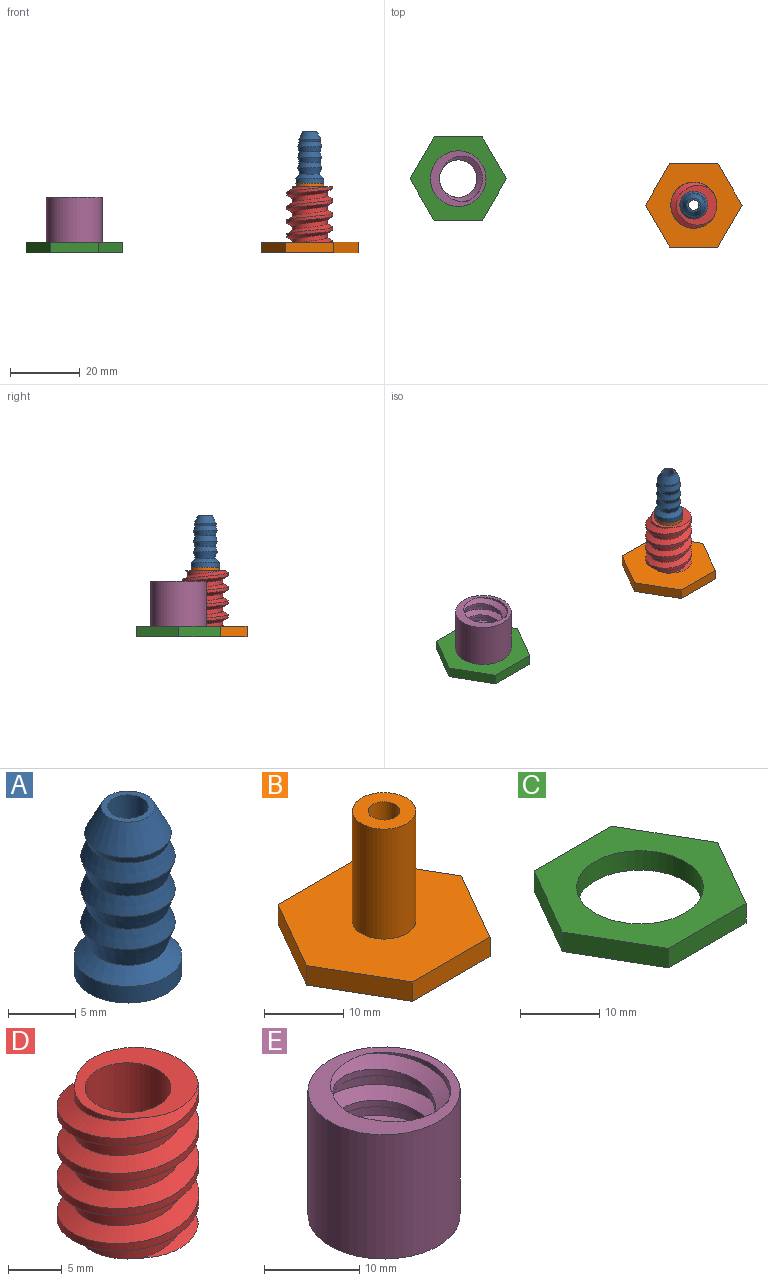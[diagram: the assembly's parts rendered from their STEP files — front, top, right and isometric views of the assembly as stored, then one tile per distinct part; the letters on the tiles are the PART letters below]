
ASSEMBLY  parts=5 mates=4
PART A: 14 faces, bbox 8x8x15 mm
  f0: cylinder r=4mm len=8mm, axis (0,0,1), area 37.7mm2, adj f2,f11
  f1: cylinder r=1.5mm len=14.2mm, axis (0,0,1), area 133.8mm2, adj f3,f12
  f2: plane 8x8mm, normal (0,0,-1), area 33.6mm2, adj f0,f12
  f3: plane 4x4mm, normal (0,0,1), area 5.5mm2, adj f1,f13
  f4: cone r=3.5mm half-angle=18.4deg, axis (0,0,1), area 12.9mm2, adj f6,f13
  f5: cone r=3.5mm half-angle=18.4deg, axis (0,0,1), area 32.3mm2, adj f6,f8
  f6: cone r=3mm half-angle=18.4deg, axis (0,0,-1), area 32.3mm2, adj f4,f5
  f7: cone r=3.5mm half-angle=18.4deg, axis (0,0,1), area 32.3mm2, adj f8,f10
  f8: cone r=3mm half-angle=18.4deg, axis (0,0,-1), area 32.3mm2, adj f5,f7
  f9: cone r=3.5mm half-angle=18.4deg, axis (0,0,1), area 39.6mm2, adj f10,f11
  f10: cone r=3mm half-angle=18.4deg, axis (0,0,-1), area 32.3mm2, adj f7,f9
  f11: cone r=2.5mm half-angle=45deg, axis (0,0,-1), area 34.4mm2, adj f0,f9
  f12: cone r=2.3mm half-angle=45deg, axis (0,0,-1), area 13.5mm2, adj f1,f2
  f13: cone r=4.9mm half-angle=27deg, axis (0,0,-1), area 43.6mm2, adj f3,f4
PART B: 11 faces, bbox 27.7x24x20 mm
  f0: plane 12x6.93mm, normal (-0.87,-0.5,0), area 41.6mm2, adj f1,f5,f6,f7
  f1: plane 13.86x3mm, normal (0,-1,0), area 41.6mm2, adj f0,f2,f6,f7
  f2: plane 12x6.93mm, normal (0.87,-0.5,0), area 41.6mm2, adj f1,f3,f6,f7
  f3: plane 12x6.93mm, normal (0.87,0.5,0), area 41.6mm2, adj f2,f4,f6,f7
  f4: plane 13.86x3mm, normal (0,1,0), area 41.6mm2, adj f3,f5,f6,f7
  f5: plane 12x6.93mm, normal (-0.87,0.5,0), area 41.6mm2, adj f0,f4,f6,f7
  f6: plane 27.71x24mm, normal (0,0,1), area 448.6mm2, adj f0,f1,f2,f3,f4,f5,f9
  f7: plane 27.71x24mm, normal (0,0,-1), area 486.3mm2, adj f0,f1,f2,f3,f4,f5,f8
  f8: cylinder r=2mm len=20mm, axis (0,0,-1), area 251.3mm2, adj f7,f10
  f9: cylinder r=4mm len=17mm, axis (0,0,-1), area 427.3mm2, adj f6,f10
  f10: plane 8x8mm, normal (0,0,1), area 37.7mm2, adj f8,f9
PART C: 9 faces, bbox 27.7x24x3 mm
  f0: plane 12x6.93mm, normal (-0.87,0.5,0), area 41.6mm2, adj f1,f6,f7,f8
  f1: plane 12x6.93mm, normal (-0.87,-0.5,0), area 41.6mm2, adj f0,f2,f7,f8
  f2: plane 13.86x3mm, normal (0,-1,0), area 41.6mm2, adj f1,f3,f7,f8
  f3: plane 12x6.93mm, normal (0.87,-0.5,0), area 41.6mm2, adj f2,f4,f7,f8
  f4: plane 12x6.93mm, normal (0.87,0.5,0), area 41.6mm2, adj f3,f6,f7,f8
  f5: cylinder r=8mm len=16mm, axis (0,0,-1), area 150.8mm2, adj f7,f8
  f6: plane 13.86x3mm, normal (0,1,0), area 41.6mm2, adj f0,f4,f7,f8
  f7: plane 27.71x24mm, normal (0,0,1), area 297.8mm2, adj f0,f1,f2,f3,f4,f5,f6
  f8: plane 27.71x24mm, normal (0,0,-1), area 297.8mm2, adj f0,f1,f2,f3,f4,f5,f6
PART D: 7 faces, bbox 13.8x15.8x19.7 mm
  f0: plane 12.16x12mm, normal (0,0,1), area 53.5mm2, adj f2,f3,f4,f5,f6
  f1: plane 12.16x12mm, normal (0,0,-1), area 53.5mm2, adj f2,f3,f4,f5,f6
  f2: cylinder r=4mm len=16mm, axis (0,0,-1), area 402.1mm2, adj f0,f1
  f3: cylinder r=5mm len=16mm, axis (0,0,1), area 164.6mm2, adj f0,f1,f4,f6
  f4: bspline ~18.92x15.24mm, area 270.5mm2, adj f0,f1,f3,f5
  f5: cylinder r=6.6mm len=16mm, axis (0,0,1), area 138.3mm2, adj f0,f1,f4,f6
  f6: bspline ~18.92x15.24mm, area 270.8mm2, adj f0,f1,f3,f5
PART E: 7 faces, bbox 16.6x16.8x19.8 mm
  f0: plane 16.65x16.65mm, normal (0,0,1), area 75.2mm2, adj f1,f3,f4,f5,f6
  f1: cylinder r=8mm len=16mm, axis (0,0,-1), area 804.2mm2, adj f0,f2
  f2: plane 16.65x16.65mm, normal (0,0,-1), area 75.2mm2, adj f1,f3,f4,f5,f6
  f3: cylinder r=7mm len=16mm, axis (0,0,1), area 232.7mm2, adj f0,f2,f4,f6
  f4: bspline ~18.92x16.17mm, area 289.3mm2, adj f0,f2,f3,f5
  f5: cylinder r=5.4mm len=16mm, axis (0,0,1), area 111.3mm2, adj f0,f2,f4,f6
  f6: bspline ~18.92x16.17mm, area 288.9mm2, adj f0,f2,f3,f5
PLACE A t=(33.95,-3.47,30.79)mm
PLACE B t=(33.95,-3.47,7.79)mm
PLACE C t=(-33.75,4.15,7.79)mm
PLACE D t=(33.95,-3.47,6.79)mm
PLACE E t=(-33.75,4.15,3.79)mm
MATE planar B.f8 <-> C.f8  axis (0,0,-1) through (33.95,-3.47,7.79)mm
MATE fastened E.f3 <-> C.f5  axis (0,0,1) through (-33.75,4.15,7.79)mm
MATE fastened A.f0 <-> B.f9  axis (0,0,-1) through (33.95,-3.47,27.79)mm
MATE fastened D.f3 <-> B.f9  axis (0,0,1) through (33.95,-3.47,10.79)mm
